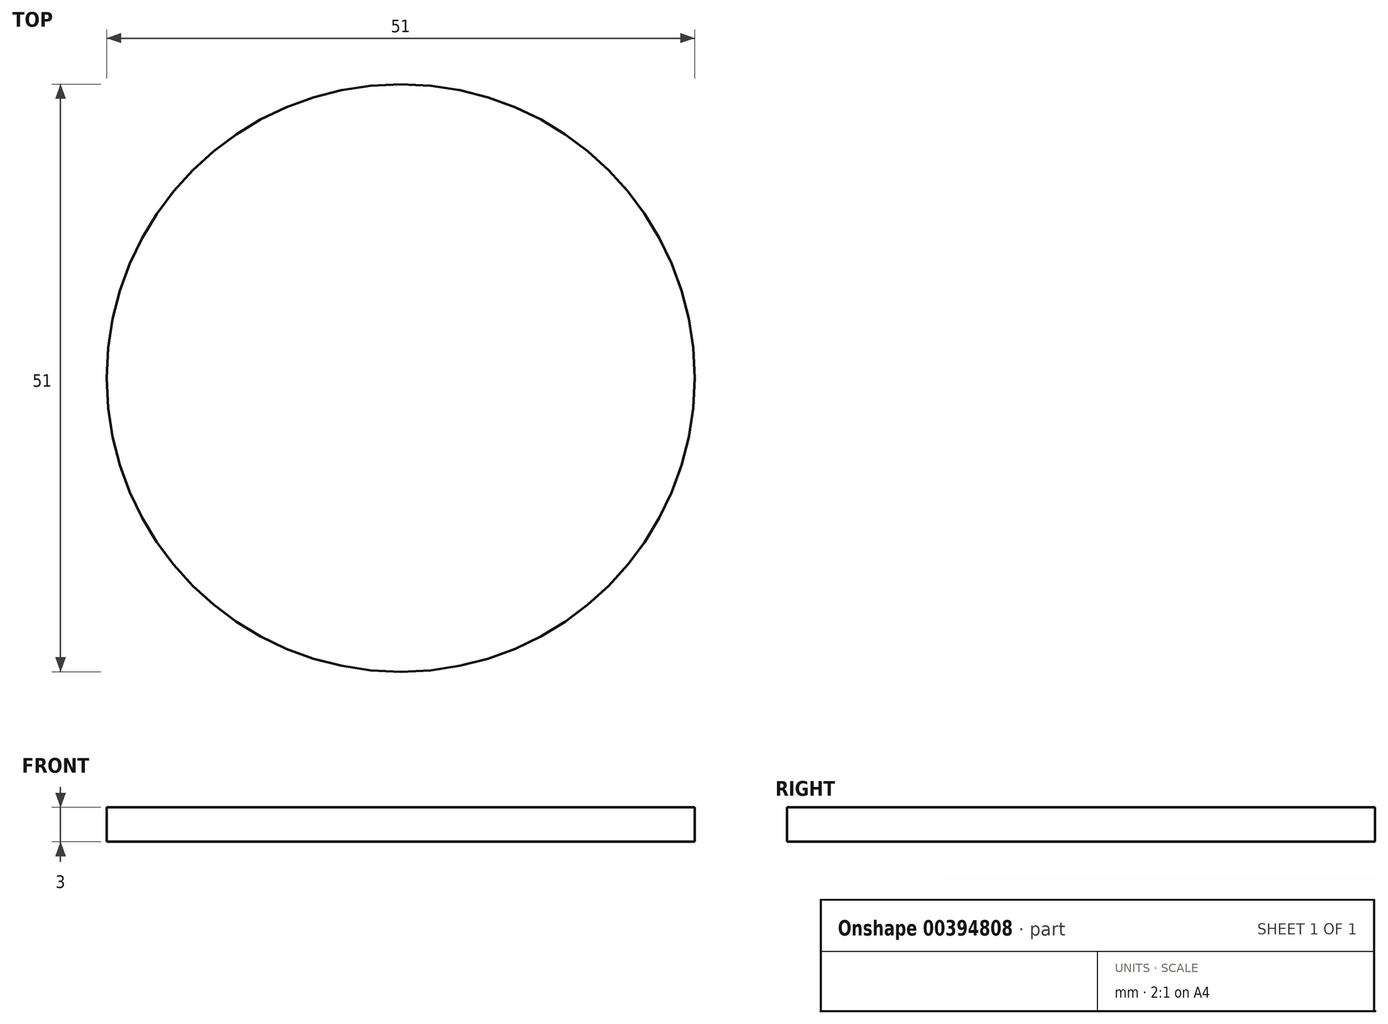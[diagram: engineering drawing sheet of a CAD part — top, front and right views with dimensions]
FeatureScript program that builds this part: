
annotation { "Feature Type Name" : "Feature", "Feature Type Description" : "" }
export const myFeature = defineFeature(function(context is Context, id is Id, definition is map)
    precondition{}
    {
        {
            var Q0;
            Q0=qCreatedBy(makeId("Top.planeOp"),FACE);
            var sketch = newSketch(context, id + "F0", { "sketchPlane" : qUnion([Q0])});
            skCircle(sketch, "E0", {"center": v(0, 0) * mm, "radius": 72 * mm});
            skSolve(sketch);
        }
        {
            var Q0;
            Q0 = qSketchRegion(id + "F0", true);
            extrude(context, id + "F1", {"entities" : qUnion([Q0]), "depth" : 3 * mm});
        }
        {
            var Q0;
            Q0=makeQuery(id+"F1.opExtrude","CAP_FACE",FACE,{"disambiguationData":[OSD([sQuery(id+"F0.wireOp",EDGE,"E0")])],"isStart":false});
            var sketch = newSketch(context, id + "F2", { "sketchPlane" : qUnion([Q0])});
            skCircle(sketch, "E1", {"center": v(-40.5, 0) * mm, "radius": 25.5 * mm});
            skLineSegment(sketch, "E2", {"start": v(0, 44.02) * mm, "end": v(0, -38.94) * mm});
            skCircle(sketch, "E3.MirrorC", {"center": v(40.5, 0) * mm, "radius": 25.5 * mm});
            skSolve(sketch);
        }
        {
            var Q0;
            Q0=makeQuery(id+"F2.imprint","IMPRINT",FACE,{"disambiguationData":[TD([[makeQuery(id+"F2.imprint","IMPRINT",EDGE,{"derivedFrom":sQuery(id+"F2.wireOp",EDGE,"E1")}),1.0]])]});
            var Q1;
            Q1=makeQuery(id+"F2.imprint","IMPRINT",FACE,{"disambiguationData":[TD([[makeQuery(id+"F2.imprint","IMPRINT",EDGE,{"derivedFrom":sQuery(id+"F2.wireOp",EDGE,"E3.MirrorC")}),-1.0]])]});
            extrude(context, id + "F3", {"entities" : qUnion([Q0, Q1]), "operationType" : NewBodyOperationType.REMOVE, "oppositeDirection" : true, "depth" : 3 * mm});
        }
        {
            var Q0;
            Q0=makeQuery(id+"F1.opExtrude","CAP_FACE",FACE,{"disambiguationData":[OSD([sQuery(id+"F0.wireOp",EDGE,"E0")])],"isStart":false});
            var sketch = newSketch(context, id + "F4", { "sketchPlane" : qUnion([Q0])});
            skCircle(sketch, "E4", {"center": v(0, 61.5) * mm, "radius": 3 * mm});
            skCircle(sketch, "E5", {"center": v(0, 0) * mm, "radius": 4.5 * mm});
            skCircle(sketch, "E6.MirrorC", {"center": v(0, -61.5) * mm, "radius": 3 * mm});
            skSolve(sketch);
        }
        {
            var Q0;
            Q0 = qSketchRegion(id + "F4", true);
            extrude(context, id + "F5", {"entities" : qUnion([Q0]), "operationType" : NewBodyOperationType.REMOVE, "oppositeDirection" : true, "depth" : 25.4 * mm});
        }
        {
            var Q0;
            Q0=makeQuery(id+"F1.opExtrude","CAP_FACE",FACE,{"disambiguationData":[OSD([sQuery(id+"F0.wireOp",EDGE,"E0")])],"isStart":false});
            var sketch = newSketch(context, id + "F6", { "sketchPlane" : qUnion([Q0])});
            skCircle(sketch, "E7", {"center": v(0, 61.5) * mm, "radius": 3 * mm});
            skCircle(sketch, "E8", {"center": v(0, 0) * mm, "radius": 61.5 * mm, "construction": true});
            skCircle(sketch, "E9.1.0", {"center": v(-53.26, -30.75) * mm, "radius": 3 * mm});
            skCircle(sketch, "E9.2.0", {"center": v(53.26, -30.75) * mm, "radius": 3 * mm});
            skSolve(sketch);
        }
        {
            var Q0;
            Q0=makeQuery(id+"F6.imprint","IMPRINT",FACE,{"disambiguationData":[TD([[makeQuery(id+"F6.imprint","IMPRINT",EDGE,{"derivedFrom":sQuery(id+"F6.wireOp",EDGE,"E9.1.0")}),1.0]])]});
            var Q1;
            Q1=makeQuery(id+"F6.imprint","IMPRINT",FACE,{"disambiguationData":[TD([[makeQuery(id+"F6.imprint","IMPRINT",EDGE,{"derivedFrom":sQuery(id+"F6.wireOp",EDGE,"E9.2.0")}),1.0]])]});
            extrude(context, id + "F7", {"entities" : qUnion([Q0, Q1]), "operationType" : NewBodyOperationType.REMOVE, "oppositeDirection" : true, "depth" : 25.4 * mm});
        }
    });
